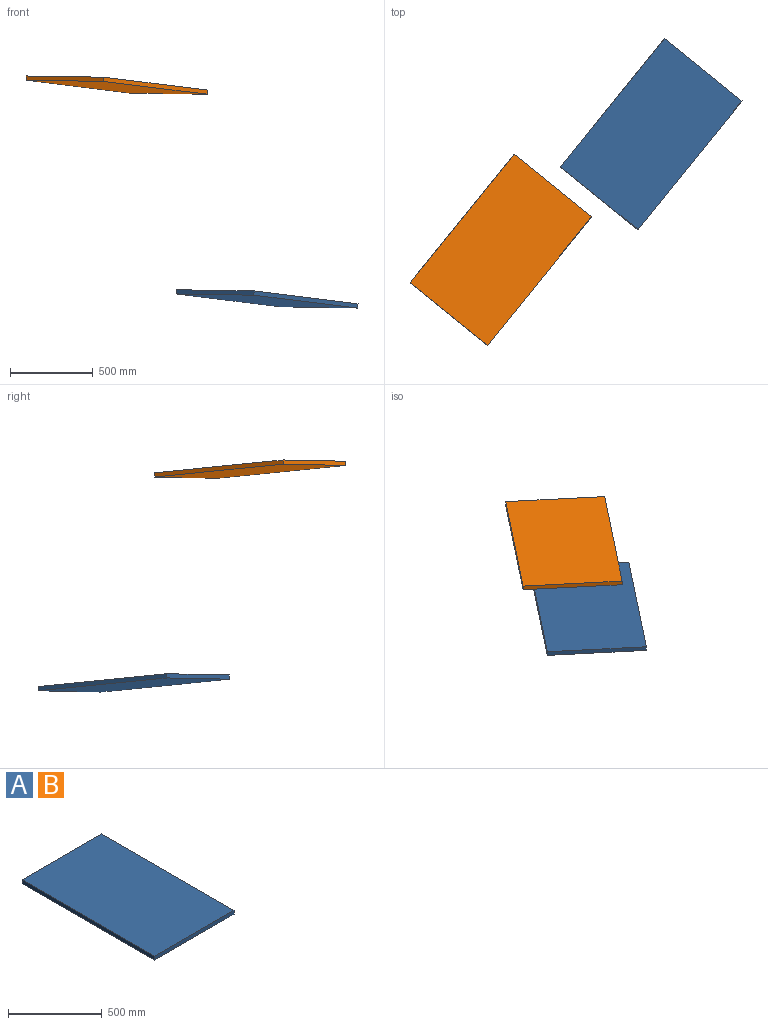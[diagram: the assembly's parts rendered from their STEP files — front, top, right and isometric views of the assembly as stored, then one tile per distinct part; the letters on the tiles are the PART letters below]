
ASSEMBLY  parts=2 mates=2
PART A: 6 faces, bbox 600x1000x25.4 mm
  f0: plane 600x25.4mm, normal (0,-1,0), area 15240mm2, adj f1,f3,f4,f5
  f1: plane 1000x25.4mm, normal (1,0,0), area 25400mm2, adj f0,f2,f4,f5
  f2: plane 600x25.4mm, normal (0,1,0), area 15240mm2, adj f1,f3,f4,f5
  f3: plane 1000x25.4mm, normal (-1,0,0), area 25400mm2, adj f0,f2,f4,f5
  f4: plane 1000x600mm, normal (0,0,1), area 600000mm2, adj f0,f1,f2,f3
  f5: plane 1000x600mm, normal (0,0,-1), area 600000mm2, adj f0,f1,f2,f3
PART B: same geometry as A
PLACE A rot(axis=(-0.1,0.06,-0.99),39.2deg) t=(479.17,381.98,-2733.98)mm
PLACE B rot(axis=(-0.1,0.06,-0.99),39.2deg) t=(-427.99,-318.69,-1445.19)mm
MATE parallel B.f4 <-> A.f5  axis (0.06,0.05,1) through (119.9,-118.27,-1462.27)mm
MATE parallel A.f1 <-> B.f1  axis (0.78,-0.63,-0.01) through (1259.5,393.02,-2767.42)mm
